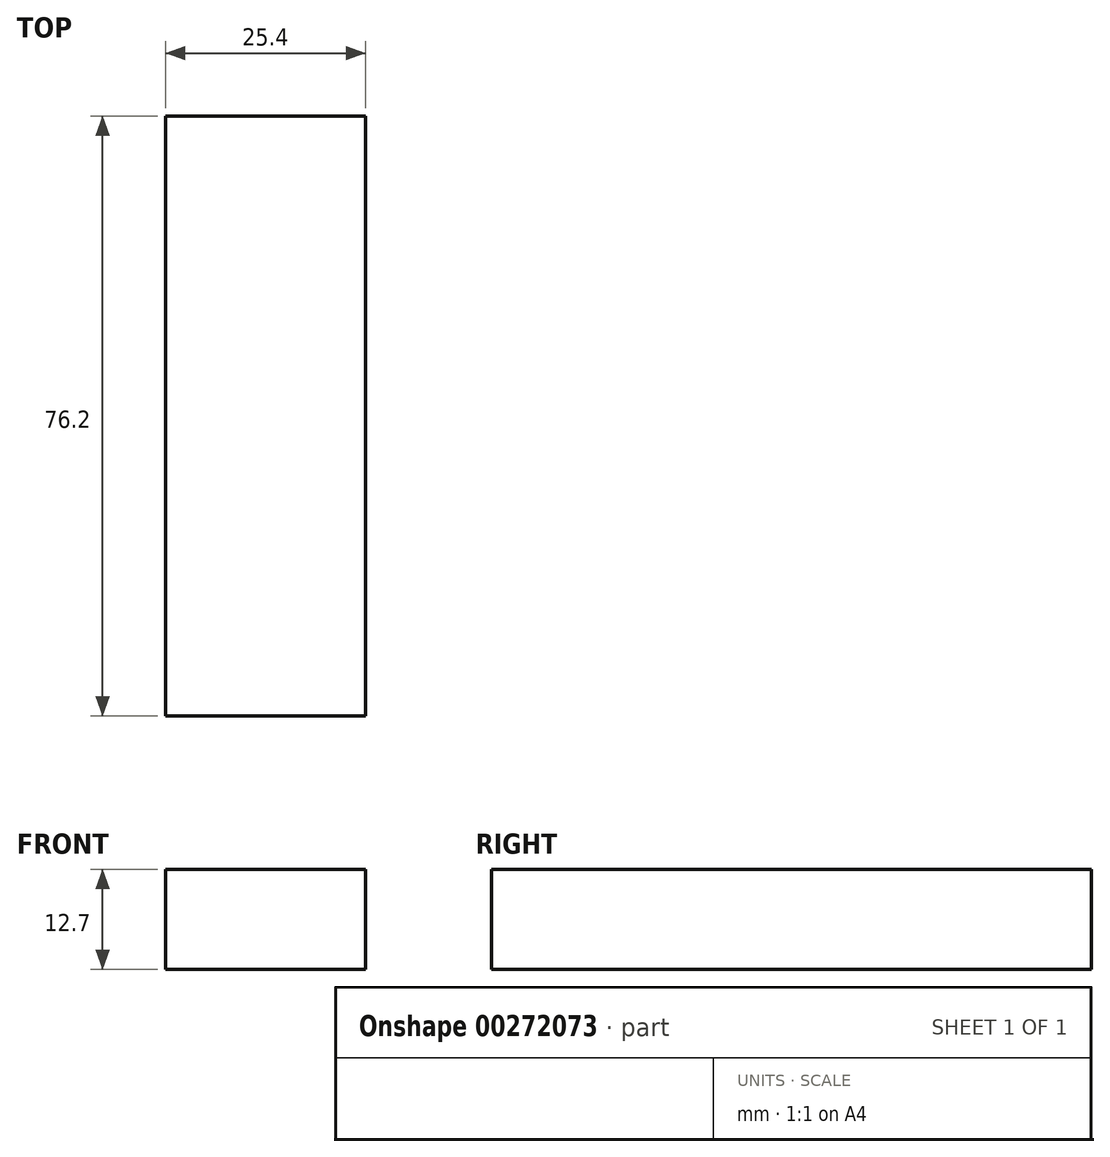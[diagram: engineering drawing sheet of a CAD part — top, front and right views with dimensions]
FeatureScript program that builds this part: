
annotation { "Feature Type Name" : "Feature", "Feature Type Description" : "" }
export const myFeature = defineFeature(function(context is Context, id is Id, definition is map)
    precondition{}
    {
        {
            var Q0;
            Q0=qCreatedBy(makeId("Front.planeOp"),FACE);
            var sketch = newSketch(context, id + "F0", { "sketchPlane" : qUnion([Q0])});
            skLineSegment(sketch, "E0.bottom", {"start": v(-40.55, 26.35) * mm, "end": v(-65.95, 26.35) * mm});
            skLineSegment(sketch, "E0.top", {"start": v(-40.55, 39.05) * mm, "end": v(-65.95, 39.05) * mm});
            skLineSegment(sketch, "E0.left", {"start": v(-40.55, 26.35) * mm, "end": v(-40.55, 39.05) * mm});
            skLineSegment(sketch, "E0.right", {"start": v(-65.95, 26.35) * mm, "end": v(-65.95, 39.05) * mm});
            skPoint(sketch, "E0.middle", {"position": v(-53.25, 32.7) * mm});
            skSolve(sketch);
        }
        {
            var Q0;
            Q0 = qSketchRegion(id + "F0", true);
            extrude(context, id + "F1", {"entities" : qUnion([Q0]), "depth" : 76.2 * mm});
        }
    });
